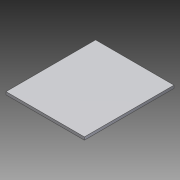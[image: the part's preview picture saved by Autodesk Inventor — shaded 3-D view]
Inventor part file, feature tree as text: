
AUTODESK INVENTOR PART (.ipt)
format: ipt  version: 2014 SP1 (Build 180222100, 222)  size: 69,120 bytes
history: native  units: in
note: dims shown in document units (in); Inventor stores cm internally (conversion verified against a paired STEP export)
features: extrude x1, sketch x1
ambient origin geometry x8: Origin, YZ Plane, XZ Plane, XY Plane, X Axis, Y Axis, Z Axis, Center Point
bodies: Solid1 (feature_tree)
feature tree (2):
  extrude  "Extrusion1"  Depth=2.0in
  sketch  "Sketch1"  dims[d0=1.75in d1=2.0in d2=0.0625in d3=0.0in]
